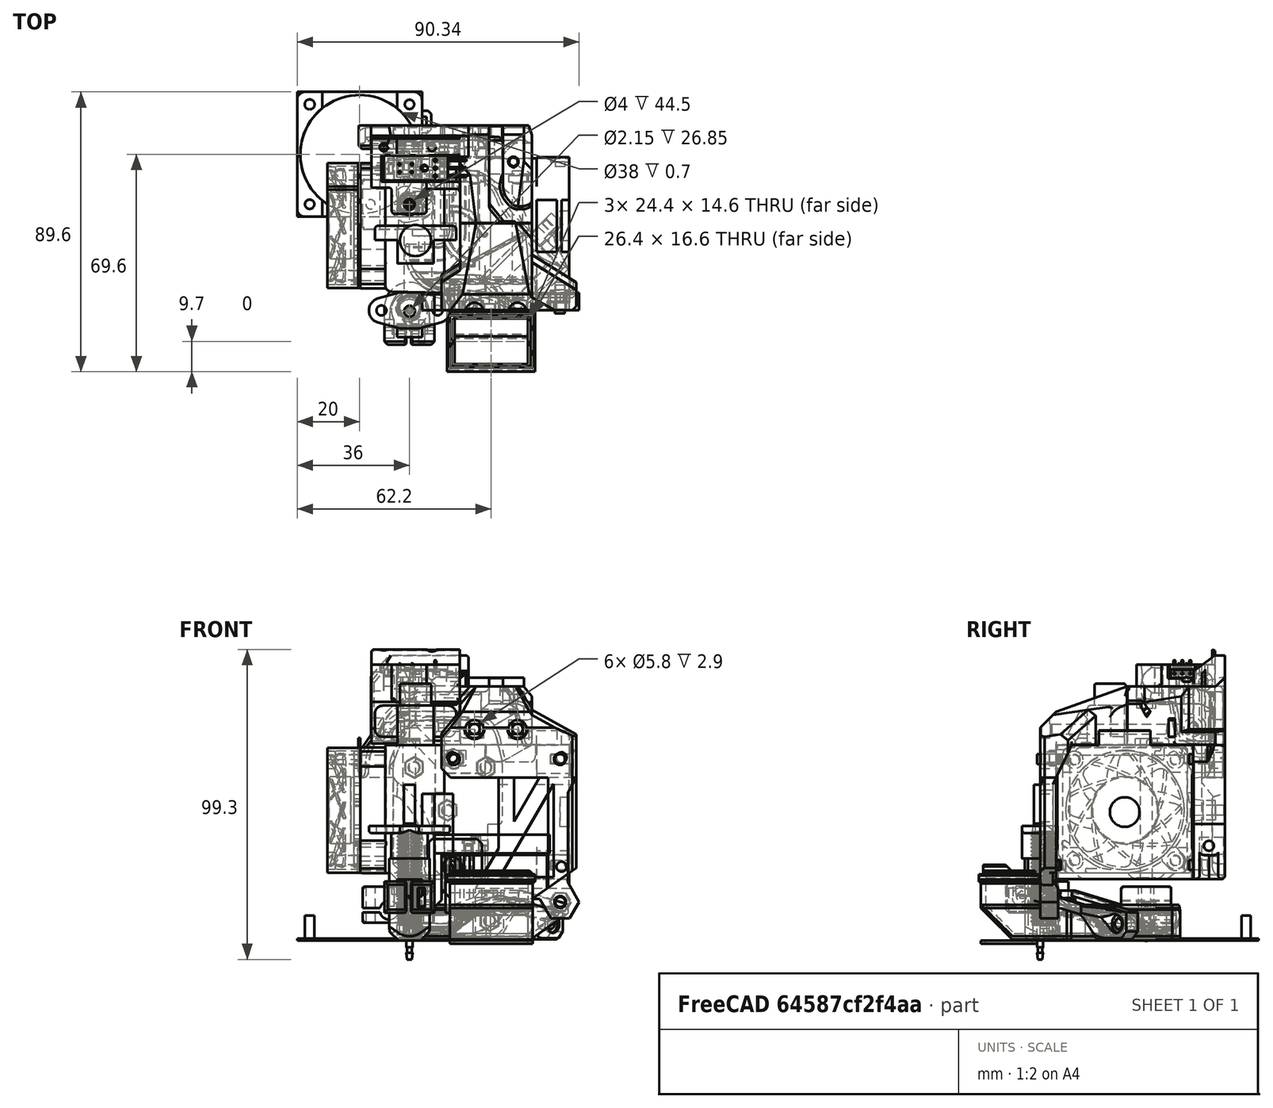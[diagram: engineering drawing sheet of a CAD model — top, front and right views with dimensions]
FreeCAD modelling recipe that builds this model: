
FCSTD DOCUMENT  (FreeCAD 0.18R14555 (Git shallow))
Label: bearmeara-4020-duct
License: All rights reserved
LicenseURL: http://en.wikipedia.org/wiki/All_rights_reserved
objects: Part::Box×57, Part::Cut×48, Part::Feature×41, Part::MultiFuse×32, Part::Cylinder×29, Part::Chamfer×24, Sketcher::SketchObject×6, PartDesign::Body×4, Part::MultiCommon×4, App::DocumentObjectGroup×3, Mesh::Feature×2, PartDesign::AdditiveLoft×2, PartDesign::Pad×2, App::Part×1
note: 253 computed .brp shape members not serialized (recipe doc carries the construction recipe); baked Part::Feature solids carry a one-line shape summary decoded from their .brp

FEATURE [Part::Feature] Part__Feature018  label="NOZZLE-POS"
  Placement = pos=(-0.025,3.1e-14,12.45) rot=(0.707107,0.707107,0;3.14159rad)
  shape: bbox 8.083 x 7 x 12.5 mm, 18 faces (baked)
FEATURE [Part::Feature] Part__Feature012  label="body_front"
  Placement = pos=(-5.275,25.1,21) rot=(0,0,-1;1.5708rad)
  shape: bbox 44.13 x 28.92 x 79.97 mm, 174 faces (baked)
FEATURE [Part::Feature] Part__Feature017  label="v6_heaterblock v1"
  Placement = pos=(-14.9885,-8.00025,5.758) rot=(0,0,1;0rad)
  shape: bbox 23 x 16 x 11.5 mm, 37 faces (baked)
FEATURE [Part::Feature] Part__Feature013  label="stepper"
  Placement = pos=(51.225,-28.9,19.7) rot=(0,0,1;1.5708rad)
  shape: bbox 40 x 44 x 47.7 mm, 101 faces (baked)
FEATURE [Part::Feature] Part__Feature014  label="heatsink"
  Placement = pos=(11.225,-28.4,19.7) rot=(0,0,1;1.5708rad)
  shape: bbox 30.92 x 43.26 x 62.61 mm, 110 faces (baked)
FEATURE [Part::Feature] Part__Feature016  label="e3d_hemera_fan v1"
  Placement = pos=(-15.775,13.2,61.8) rot=(0.57735,-0.57735,0.57735;4.18879rad)
  shape: bbox 10.51 x 40.01 x 40.01 mm, 129 faces (baked)
FEATURE [Mesh::Feature] lower_4020_fan_duct  label="lower_4020-fan-duct"
  Placement = pos=(11.3,-33.9,19.8) rot=(0,0,1;0rad)
FEATURE [Part::Feature] Cut007002001001  label="fan-mount-frame001"
  shape: bbox 28.2 x 19.2 x 3.5 mm, 16 faces (baked)
FEATURE [Part::Feature] Part__Feature  label="duct001"
  Placement = pos=(13,-15,0) rot=(0,0,1;0rad)
  shape: bbox 62.87 x 53.67 x 16.75 mm, 145 faces (baked)
FEATURE [Part::Feature] Part__Feature025  label="duct002"
  Placement = pos=(13,-15,0) rot=(0,0,1;0rad)
  shape: bbox 62.87 x 53.67 x 16.75 mm, 145 faces (baked)
FEATURE [Part::Box] Box  label="Cube"
  AttacherType = Attacher::AttachEngine3D
  Height = 17
  Length = 29
  Placement = pos=(26,-38,0) rot=(0,0,1;0rad)
  Width = 48
FEATURE [Part::Box] Box001  label="Cube001"
  AttacherType = Attacher::AttachEngine3D
  Height = 27
  Length = 26
  Placement = pos=(0,-34,0) rot=(0,0,1;0rad)
  Width = 10
FEATURE [Part::Cut] Cut
  Base = -> Part__Feature
  Tool = -> Box
FEATURE [Part::Cut] Cut007002001002
  Base = -> Cut
  Placement = pos=(0,0,-0.45) rot=(0,0,1;0rad)
  Tool = -> Box001
FEATURE [Part::Box] Box002  label="Cube002"
  AttacherType = Attacher::AttachEngine3D
  Height = 2
  Length = 13
  Placement = pos=(13,-24,0.8) rot=(0,0,1;0rad)
  Width = 4
FEATURE [Part::Box] Box003  label="Cube003"
  AttacherType = Attacher::AttachEngine3D
  Height = 1
  Length = 5
  Placement = pos=(21,-24,0.8) rot=(0,0,1;0rad)
  Width = 13
FEATURE [Part::Cut] Cut007002001003
  Base = -> Cut007002001002
  Tool = -> Box002
FEATURE [Part::Cut] Cut007002001004
  Base = -> Cut007002001003
  Tool = -> Box003
FEATURE [Part::Box] Box004  label="Cube004"
  AttacherType = Attacher::AttachEngine3D
  Height = 10
  Length = 24
  Placement = pos=(7,-30,10) rot=(0,0,1;0rad)
  Width = 27
FEATURE [Part::Cut] Cut007002001005
  Base = -> Cut007002001004
  Tool = -> Box004
FEATURE [Part::Box] Box005  label="Cube005"
  AttacherType = Attacher::AttachEngine3D
  Height = 10
  Length = 32
  Placement = pos=(-2,-38,0) rot=(0,0,1;0rad)
  Width = 14
FEATURE [Part::Box] Box007  label="Cube007"
  AttacherType = Attacher::AttachEngine3D
  Height = 10
  Length = 21
  Placement = pos=(26,-24,0) rot=(0,0,1;0rad)
  Width = 21
FEATURE [Part::Box] Box008  label="Cube008"
  AttacherType = Attacher::AttachEngine3D
  Height = 1
  Length = 41
  Placement = pos=(10,-35,9) rot=(0,0,1;0.506145rad)
  Width = 10
FEATURE [Part::MultiFuse] Fusion
  Shapes = -> [Cut007002001005,Box008]
FEATURE [Part::Cut] Cut007002001006
  Base = -> Fusion
  Tool = -> Box005
FEATURE [Part::Cut] Cut007002001007  label="duct-square-cut"
  Base = -> Cut007002001006
  Tool = -> Box007
FEATURE [Part::Feature] Cut007002001007001  label="Cut007002001008"
  shape: bbox 41.3 x 51.61 x 10 mm, 88 faces (baked)
FEATURE [Part::Box] Box012  label="Cube012"
  AttacherType = Attacher::AttachEngine3D
  Height = 1
  Length = 26.5
  Placement = pos=(13,-53,0) rot=(0,0,1;0rad)
  Width = 18
FEATURE [Part::Box] Box013  label="Cube013"
  AttacherType = Attacher::AttachEngine3D
  Height = 1
  Length = 23.5
  Placement = pos=(14.5,-51.5,0) rot=(0,0,1;0rad)
  Width = 15
FEATURE [Part::Cut] Cut007002001007002
  Base = -> Box012
  Placement = pos=(0,0,-1) rot=(0,0,1;0rad)
  Tool = -> Box013
FEATURE [Sketcher::SketchObject] Sketch
  AttachmentOffset = pos=(0,0,19) rot=(0,0,1;0rad)
  MapMode = 5
  Placement = pos=(0,0,19) rot=(0,0,1;0rad)
  Support = -> [XY_Plane]
  sketch-geometry (8):
    g0: LineSegment StartX=13 StartY=-35 StartZ=0 EndX=39.5 EndY=-35 EndZ=0
    g1: LineSegment StartX=39.5 StartY=-35 StartZ=0 EndX=39.5 EndY=-53 EndZ=0
    g2: LineSegment StartX=39.5 StartY=-53 StartZ=0 EndX=13 EndY=-53 EndZ=0
    g3: LineSegment StartX=13 StartY=-53 StartZ=0 EndX=13 EndY=-35 EndZ=0
    g4: LineSegment StartX=14.5 StartY=-36.5 StartZ=0 EndX=38 EndY=-36.5 EndZ=0
    g5: LineSegment StartX=38 StartY=-36.5 StartZ=0 EndX=38 EndY=-51.5 EndZ=0
    g6: LineSegment StartX=38 StartY=-51.5 StartZ=0 EndX=14.5 EndY=-51.5 EndZ=0
    g7: LineSegment StartX=14.5 StartY=-51.5 StartZ=0 EndX=14.5 EndY=-36.5 EndZ=0
  constraints (16):
    c: Coincident(g0,g1)
    c: Coincident(g1,g2)
    c: Coincident(g2,g3)
    c: Coincident(g3,g0)
    c: Horizontal(g0)
    c: Horizontal(g2)
    c: Vertical(g1)
    c: Vertical(g3)
    c: Coincident(g4,g5)
    c: Coincident(g5,g6)
    c: Coincident(g6,g7)
    c: Coincident(g7,g4)
    c: Horizontal(g4)
    c: Horizontal(g6)
    c: Vertical(g5)
    c: Vertical(g7)
FEATURE [Sketcher::SketchObject] Sketch001
  AttachmentOffset = pos=(0,0,10.45) rot=(0,0,1;0rad)
  MapMode = 5
  Placement = pos=(0,0,10.45) rot=(0,0,1;0rad)
  Support = -> [XY_Plane]
  sketch-geometry (8):
    g0: LineSegment StartX=13 StartY=-53 StartZ=0 EndX=39.5 EndY=-53 EndZ=0
    g1: LineSegment StartX=39.5 StartY=-53 StartZ=0 EndX=39.5 EndY=-24 EndZ=0
    g2: LineSegment StartX=39.5 StartY=-24 StartZ=0 EndX=13 EndY=-24 EndZ=0
    g3: LineSegment StartX=13 StartY=-24 StartZ=0 EndX=13 EndY=-53 EndZ=0
    g4: LineSegment StartX=38 StartY=-25.5 StartZ=0 EndX=14.5 EndY=-25.5 EndZ=0
    g5: LineSegment StartX=14.5 StartY=-25.5 StartZ=0 EndX=14.5 EndY=-51.5 EndZ=0
    g6: LineSegment StartX=14.5 StartY=-51.5 StartZ=0 EndX=38 EndY=-51.5 EndZ=0
    g7: LineSegment StartX=38 StartY=-51.5 StartZ=0 EndX=38 EndY=-25.5 EndZ=0
  constraints (16):
    c: Coincident(g0,g1)
    c: Coincident(g1,g2)
    c: Coincident(g2,g3)
    c: Coincident(g3,g0)
    c: Horizontal(g0)
    c: Horizontal(g2)
    c: Vertical(g1)
    c: Vertical(g3)
    c: Coincident(g4,g5)
    c: Coincident(g5,g6)
    c: Coincident(g6,g7)
    c: Coincident(g7,g4)
    c: Horizontal(g4)
    c: Horizontal(g6)
    c: Vertical(g5)
    c: Vertical(g7)
FEATURE [PartDesign::AdditiveLoft] AdditiveLoft
  Closed = false
  Profile = -> Sketch
  Ruled = false
  Sections = -> [Sketch001]
FEATURE [PartDesign::Body] Body  label="ramp"
  Group = -> [Sketch,Sketch001,AdditiveLoft]
  Origin = -> Origin
  Tip = -> AdditiveLoft
FEATURE [Part::Feature] Body001  label="ramp001"
  Placement = pos=(0,0,-0.45) rot=(0,0,1;0rad)
  shape: bbox 26.5 x 29 x 8.55 mm, 10 faces (baked)
FEATURE [Sketcher::SketchObject] Sketch002  label="Sketch003"
  AttachmentOffset = pos=(0,0,0.45) rot=(0,0,1;0rad)
  MapMode = 5
  Placement = pos=(0,0,0.45) rot=(0,0,1;0rad)
  Support = -> [XY_Plane001]
  sketch-geometry (8):
    g0: LineSegment StartX=39.5 StartY=-24 StartZ=0 EndX=13 EndY=-24 EndZ=0
    g1: LineSegment StartX=13 StartY=-24 StartZ=0 EndX=13 EndY=-43 EndZ=0
    g2: LineSegment StartX=13 StartY=-43 StartZ=0 EndX=39.5 EndY=-43 EndZ=0
    g3: LineSegment StartX=39.5 StartY=-43 StartZ=0 EndX=39.5 EndY=-24 EndZ=0
    g4: LineSegment StartX=38 StartY=-25.5 StartZ=0 EndX=14.5 EndY=-25.5 EndZ=0
    g5: LineSegment StartX=14.5 StartY=-25.5 StartZ=0 EndX=14.5 EndY=-41.5 EndZ=0
    g6: LineSegment StartX=14.5 StartY=-41.5 StartZ=0 EndX=38 EndY=-41.5 EndZ=0
    g7: LineSegment StartX=38 StartY=-41.5 StartZ=0 EndX=38 EndY=-25.5 EndZ=0
  constraints (16):
    c: Coincident(g0,g1)
    c: Coincident(g1,g2)
    c: Coincident(g2,g3)
    c: Coincident(g3,g0)
    c: Horizontal(g0)
    c: Horizontal(g2)
    c: Vertical(g1)
    c: Vertical(g3)
    c: Coincident(g4,g5)
    c: Coincident(g5,g6)
    c: Coincident(g6,g7)
    c: Coincident(g7,g4)
    c: Horizontal(g4)
    c: Horizontal(g6)
    c: Vertical(g5)
    c: Vertical(g7)
FEATURE [Sketcher::SketchObject] Sketch003  label="Sketch004"
  AttachmentOffset = pos=(0,0,10.45) rot=(0,0,1;0rad)
  MapMode = 5
  Placement = pos=(0,0,10.45) rot=(0,0,1;0rad)
  Support = -> [XY_Plane001]
  sketch-geometry (8):
    g0: LineSegment StartX=13 StartY=-24 StartZ=0 EndX=39.5 EndY=-24 EndZ=0
    g1: LineSegment StartX=39.5 StartY=-24 StartZ=0 EndX=39.5 EndY=-53 EndZ=0
    g2: LineSegment StartX=39.5 StartY=-53 StartZ=0 EndX=13 EndY=-53 EndZ=0
    g3: LineSegment StartX=13 StartY=-53 StartZ=0 EndX=13 EndY=-24 EndZ=0
    g4: LineSegment StartX=14.5 StartY=-25.5 StartZ=0 EndX=38 EndY=-25.5 EndZ=0
    g5: LineSegment StartX=38 StartY=-25.5 StartZ=0 EndX=38 EndY=-51.5 EndZ=0
    g6: LineSegment StartX=38 StartY=-51.5 StartZ=0 EndX=14.5 EndY=-51.5 EndZ=0
    g7: LineSegment StartX=14.5 StartY=-51.5 StartZ=0 EndX=14.5 EndY=-25.5 EndZ=0
  constraints (16):
    c: Coincident(g0,g1)
    c: Coincident(g1,g2)
    c: Coincident(g2,g3)
    c: Coincident(g3,g0)
    c: Horizontal(g0)
    c: Horizontal(g2)
    c: Vertical(g1)
    c: Vertical(g3)
    c: Coincident(g4,g5)
    c: Coincident(g5,g6)
    c: Coincident(g6,g7)
    c: Coincident(g7,g4)
    c: Horizontal(g4)
    c: Horizontal(g6)
    c: Vertical(g5)
    c: Vertical(g7)
FEATURE [PartDesign::AdditiveLoft] AdditiveLoft001
  Closed = false
  Profile = -> Sketch003
  Ruled = false
  Sections = -> [Sketch002]
FEATURE [PartDesign::Body] Body002  label="lower-ramp"
  Group = -> [Sketch002,Sketch003,AdditiveLoft001]
  Origin = -> Origin001
  Tip = -> AdditiveLoft001
FEATURE [Part::Feature] Body002002  label="lower-ramp002"
  Placement = pos=(0,0,-0.45) rot=(0,0,1;0rad)
  shape: bbox 26.5 x 29 x 10 mm, 10 faces (baked)
FEATURE [Sketcher::SketchObject] Sketch004  label="Sketch005"
  MapMode = 5
  Support = -> [XY_Plane002]
  sketch-geometry (31):
    g0: GeomPoint X=26 Y=-24 Z=0
    g1: LineSegment StartX=26 StartY=-24 StartZ=0 EndX=1.71 EndY=-24 EndZ=0
    g2: LineSegment StartX=26 StartY=-24 StartZ=0 EndX=26 EndY=8.3 EndZ=0
    g3: LineSegment StartX=13 StartY=-31 StartZ=0 EndX=14.5 EndY=-31 EndZ=0
    g4: LineSegment StartX=14.5 StartY=-31 StartZ=0 EndX=14.5 EndY=-25.5 EndZ=0
    g5: LineSegment StartX=14.5 StartY=-25.5 StartZ=0 EndX=39.5 EndY=-25.5 EndZ=0
    g6: LineSegment StartX=39.5 StartY=-25.5 StartZ=0 EndX=39.5 EndY=-24 EndZ=0
    g7-g12: Circle [constr] x6 (B-spline internal-alignment scaffolding for g13; pole/knot coordinates omitted)
    g13: BSplineCurve PolesCount=6 KnotsCount=4 Degree=3 IsPeriodic=0
    g14-g17: GeomPoint [constr] x4 (B-spline internal-alignment scaffolding for g13; pole/knot coordinates omitted)
    g18-g24: Circle [constr] x7 (B-spline internal-alignment scaffolding for g25; pole/knot coordinates omitted)
    g25: BSplineCurve PolesCount=7 KnotsCount=5 Degree=3 IsPeriodic=0
    g26-g30: GeomPoint [constr] x5 (B-spline internal-alignment scaffolding for g25; pole/knot coordinates omitted)
  constraints (24):
    c: DistanceY(g0,g-1) = 24
    c: DistanceX(g-1,g0) = 26
    c: Coincident(g1,g0)
    c: Horizontal(g1)
    c: Coincident(g2,g0)
    c: Vertical(g2)
    c: Coincident(g3,g4)
    c: Vertical(g4)
    c: Coincident(g4,g5)
    c: Horizontal(g5)
    c: Coincident(g5,g6)
    c: DistanceY(g2,g2) = 32.3
    c: Coincident(g13,g1)
    c: Radius(g7) = 0.6
    c: Equal(g7, g8-g12) x5
    c: Coincident(g13,g3)
    c: InternalAlignment(g7-g12 -> g13) x6
    c: InternalAlignment(g14-g17 -> g13) x4
    c: Coincident(g25,g2)
    c: Radius(g18) = 1
    c: Equal(g18, g19-g24) x6
    c: Coincident(g25,g6)
    c: InternalAlignment(g18-g24 -> g25) x7
    c: InternalAlignment(g26-g30 -> g25) x5
FEATURE [PartDesign::Pad] Pad
  Length = 10
  Length2 = 100
  Profile = -> Sketch004
  Type = 0
FEATURE [PartDesign::Body] Body002003  label="outer"
  Group = -> [Sketch004,Pad]
  Origin = -> Origin002
  Tip = -> Pad
FEATURE [Sketcher::SketchObject] Sketch005  label="Sketch006"
  MapMode = 5
  Support = -> [XY_Plane003]
  sketch-geometry (29):
    g0: GeomPoint X=26 Y=-24 Z=0
    g1: LineSegment StartX=26 StartY=-24 StartZ=0 EndX=3.42 EndY=-24 EndZ=0
    g2: LineSegment StartX=26 StartY=-24 StartZ=0 EndX=26 EndY=6.6 EndZ=0
    g3: GeomPoint X=14.5 Y=-30 Z=0
    g4: GeomPoint X=38 Y=-25.5 Z=0
    g5-g10: Circle [constr] x6 (B-spline internal-alignment scaffolding for g11; pole/knot coordinates omitted)
    g11: BSplineCurve PolesCount=6 KnotsCount=4 Degree=3 IsPeriodic=0
    g12-g15: GeomPoint [constr] x4 (B-spline internal-alignment scaffolding for g11; pole/knot coordinates omitted)
    g16-g21: Circle [constr] x6 (B-spline internal-alignment scaffolding for g22; pole/knot coordinates omitted)
    g22: BSplineCurve PolesCount=6 KnotsCount=4 Degree=3 IsPeriodic=0
    g23-g26: GeomPoint [constr] x4 (B-spline internal-alignment scaffolding for g22; pole/knot coordinates omitted)
    g27: LineSegment StartX=14.5 StartY=-30 StartZ=0 EndX=14.5 EndY=-25.5 EndZ=0
    g28: LineSegment StartX=14.5 StartY=-25.5 StartZ=0 EndX=38 EndY=-25.5 EndZ=0
  constraints (29):
    c: DistanceY(g0,g-1) = 24
    c: DistanceX(g-1,g0) = 26
    c: Coincident(g1,g0)
    c: Horizontal(g1)
    c: Coincident(g2,g0)
    c: Vertical(g2)
    c: DistanceY(g2,g2) = 30.6
    c: DistanceX(g1,g1) = 22.58
    c: DistanceY(g4,g-1) = 25.5
    c: DistanceX(g-1,g4) = 38
    c: DistanceY(g3,g-1) = 30
    c: DistanceX(g-1,g3) = 14.5
    c: Coincident(g11,g1)
    c: Radius(g5) = 0.4
    c: Equal(g5, g6-g10) x5
    c: Coincident(g11,g3)
    c: InternalAlignment(g5-g10 -> g11) x6
    c: InternalAlignment(g12-g15 -> g11) x4
    c: Coincident(g22,g2)
    c: Radius(g16) = 1
    c: Equal(g16, g17-g21) x5
    c: Coincident(g22,g4)
    c: InternalAlignment(g16-g21 -> g22) x6
    c: InternalAlignment(g23-g26 -> g22) x4
    c: Coincident(g27,g3)
    c: Vertical(g27)
    c: Coincident(g28,g27)
    c: Coincident(g28,g4)
    c: Horizontal(g28)
FEATURE [PartDesign::Pad] Pad001
  Length = 8.2
  Length2 = 100
  Profile = -> Sketch005
  Type = 0
FEATURE [PartDesign::Body] Body002004  label="inner"
  Group = -> [Sketch005,Pad001]
  Origin = -> Origin003
  Tip = -> Pad001
FEATURE [App::DocumentObjectGroup] Group001  label="Sketch002"
  Group = -> [Body,Body002,Body002003,Body002004]
FEATURE [Part::Feature] Body002004001  label="inner001"
  Placement = pos=(0,0,0.8) rot=(0,0,1;0rad)
  shape: bbox 34.69 x 36.6 x 8.2 mm, 8 faces (baked)
FEATURE [Part::Box] Box015  label="Cube015"
  AttacherType = Attacher::AttachEngine3D
  Height = 8.2
  Length = 23.5
  Placement = pos=(14.5,-27,0.8) rot=(0,0,1;0rad)
  Width = 5
FEATURE [Part::Box] Box016  label="Cube016"
  AttacherType = Attacher::AttachEngine3D
  Height = 0.8
  Length = 23.5
  Placement = pos=(14.5,-42.5,0) rot=(0,0,1;0rad)
  Width = 18
FEATURE [Part::Feature] Body002003001  label="outer001"
  shape: bbox 37.79 x 39.3 x 10 mm, 10 faces (baked)
FEATURE [Part::Feature] Body002004002  label="inner002"
  Placement = pos=(0,0,0.8) rot=(0,0,1;0rad)
  shape: bbox 34.69 x 36.6 x 8.2 mm, 8 faces (baked)
FEATURE [Part::Feature] Cut007002001007009  label="fan-mount-frame002"
  Placement = pos=(0,0,-0.45) rot=(0,0,1;0rad)
  shape: bbox 28.2 x 19.2 x 3.5 mm, 16 faces (baked)
FEATURE [Part::Cut] Cut007002001007010
  Base = -> Body002003001
  Tool = -> Body002004001
FEATURE [Part::MultiFuse] Fusion001
  Shapes = -> [Box016,Body002002]
FEATURE [Part::Cut] Cut007002001007011
  Base = -> Fusion001
  Tool = -> Box015
FEATURE [Part::Cut] Cut007002001007012
  Base = -> Cut007002001007011
  Tool = -> Body002004002
FEATURE [Part::MultiFuse] Fusion002
  Shapes = -> [Body001,Cut007002001007012]
FEATURE [Part::MultiFuse] Fusion003
  Shapes = -> [Fusion002,Cut007002001007010]
FEATURE [Part::MultiFuse] Fusion004
  Placement = pos=(0,0,1) rot=(0,0,1;0rad)
  Shapes = -> [Fusion003,Cut007002001007001]
FEATURE [Part::Box] Box017  label="Cube017"
  AttacherType = Attacher::AttachEngine3D
  Height = 0.8
  Length = 4
  Placement = pos=(10,-25,1.8) rot=(0,0,1;0rad)
  Width = 4
FEATURE [Part::Box] Box018  label="Cube018"
  AttacherType = Attacher::AttachEngine3D
  Height = 1
  Length = 36.5
  Placement = pos=(5.64694,-26.4947,8.5) rot=(0,0,1;0.488692rad)
  Width = 1
FEATURE [Part::Box] Box019  label="Cube019"
  AttacherType = Attacher::AttachEngine3D
  Height = 1
  Length = 35.5
  Placement = pos=(3.75,-25.25,9.1) rot=(0,0,1;0rad)
  Width = 1
FEATURE [Part::Chamfer] Chamfer005
  Base = -> Box018
  Edges = 1 edges r=0.5: [Edge9]
  Placement = pos=(0,0,1) rot=(0,0,1;0rad)
FEATURE [Part::Cylinder] Cylinder001  label="stepper-screw-pos"
  Angle = 360
  AttacherType = Attacher::AttachEngine3D
  Height = 10
  Placement = pos=(48.73,-25,58.7) rot=(1,0,0;1.5708rad)
  Radius = 1.65
FEATURE [Part::Cylinder] Cylinder002  label="fill"
  Angle = 360
  AttacherType = Attacher::AttachEngine3D
  Height = 5
  Placement = pos=(48.23,-28.9,58.2) rot=(1,0,0;1.5708rad)
  Radius = 3
FEATURE [Part::Cylinder] Cylinder003  label="fill001"
  Angle = 360
  AttacherType = Attacher::AttachEngine3D
  Height = 5
  Placement = pos=(14.23,-28.9,58.2) rot=(1,0,0;1.5708rad)
  Radius = 3
FEATURE [Part::Box] Box020  label="Cube020"
  AttacherType = Attacher::AttachEngine3D
  Height = 4
  Length = 4
  Placement = pos=(10,-28.9,56) rot=(0,0,1;0rad)
  Width = 3
FEATURE [Part::Box] Box021  label="Cube021"
  AttacherType = Attacher::AttachEngine3D
  Height = 6
  Length = 4
  Placement = pos=(48.55,-28.9,55.2) rot=(0,0,1;0rad)
  Width = 5
FEATURE [Part::Cylinder] Cylinder004  label="stepper-screw-pos001"
  Angle = 360
  AttacherType = Attacher::AttachEngine3D
  Height = 10
  Placement = pos=(13.73,-25,58.7) rot=(1,0,0;1.5708rad)
  Radius = 1.65
FEATURE [Part::Cylinder] Cylinder005  label="stepper-screw-pos002"
  Angle = 360
  AttacherType = Attacher::AttachEngine3D
  Height = 10
  Placement = pos=(48.23,-25,58.2) rot=(1,0,0;1.5708rad)
  Radius = 1.6
FEATURE [Part::Cylinder] Cylinder006  label="stepper-screw-pos003"
  Angle = 360
  AttacherType = Attacher::AttachEngine3D
  Height = 10
  Placement = pos=(13.73,-25,25.1) rot=(1,0,0;1.5708rad)
  Radius = 0.5
FEATURE [Part::Cylinder] Cylinder007  label="stepper-screw-pos004"
  Angle = 360
  AttacherType = Attacher::AttachEngine3D
  Height = 10
  Placement = pos=(48.73,-25,23.7) rot=(1,0,0;1.5708rad)
  Radius = 1.6
FEATURE [Part::Feature] Part__Feature012001  label="body_front001"
  Placement = pos=(-5.275,25.1,21) rot=(0,0,-1;1.5708rad)
  shape: bbox 44.13 x 28.92 x 79.97 mm, 174 faces (baked)
FEATURE [Part::Feature] Part__Feature012002  label="body_front002"
  Placement = pos=(-5.275,25.1,21) rot=(0,0,-1;1.5708rad)
  shape: bbox 44.13 x 28.92 x 79.97 mm, 174 faces (baked)
FEATURE [Part::MultiFuse] Fusion008
  Shapes = -> [Part__Feature012002,Cylinder003]
FEATURE [Part::MultiFuse] Fusion009
  Shapes = -> [Fusion008,Cylinder002]
FEATURE [Part::Cut] Cut007002001007014
  Base = -> Fusion009
  Tool = -> Box020
FEATURE [Part::Cut] Cut007002001007015
  Base = -> Cut007002001007014
  Tool = -> Box021
FEATURE [Part::Cut] Cut007002001007016
  Base = -> Cut007002001007015
  Tool = -> Cylinder001
FEATURE [Part::Cut] Cut007002001007017
  Base = -> Cut007002001007016
  Tool = -> Cylinder004
FEATURE [Part::Box] Box022  label="Cube022"
  AttacherType = Attacher::AttachEngine3D
  Height = 5
  Length = 7
  Placement = pos=(11,-31,56) rot=(0,0,1;0rad)
  Width = 10
FEATURE [Part::MultiCommon] Common  label="body-pos-fix"
  Shapes = -> [Box022,Part__Feature012001]
FEATURE [Part::Feature] Common001  label="body-pos-fix001"
  Placement = pos=(0,0,-34) rot=(0,0,1;0rad)
  shape: bbox 7 x 3.1 x 5 mm, 23 faces (baked)
FEATURE [Part::Box] Box023  label="Cube023"
  AttacherType = Attacher::AttachEngine3D
  Height = 10
  Length = 10
  Placement = pos=(4,-28.9,19) rot=(0,0,1;0rad)
  Width = 10
FEATURE [Part::Cut] Cut007002001007018
  Base = -> Common001
  Tool = -> Box023
FEATURE [Part::Cylinder] Cylinder008  label="tmpp"
  Angle = 360
  AttacherType = Attacher::AttachEngine3D
  Height = 2.1
  Placement = pos=(14.23,-28.9,24.2) rot=(1,0,0;1.5708rad)
  Radius = 1.7
FEATURE [Part::MultiFuse] Fusion010  label="body-pos-2"
  Shapes = -> [Cylinder008,Cut007002001007018]
FEATURE [Part::Box] Box024  label="Cube024"
  AttacherType = Attacher::AttachEngine3D
  Height = 14
  Length = 41
  Placement = pos=(10.23,-33.9,13.5) rot=(0,0,1;0rad)
  Width = 5
FEATURE [Part::Cylinder] Cylinder009  label="stepper-screw-pos005"
  Angle = 360
  AttacherType = Attacher::AttachEngine3D
  Height = 12
  Placement = pos=(13.73,-31,26.4) rot=(1,0,0;1.5708rad)
  Radius = 0.5
FEATURE [Part::Feature] Fusion010002  label="body-pos-1"
  Placement = pos=(62.4,0,48.4) rot=(0,1,0;3.14159rad)
  shape: bbox 7 x 3.1 x 5 mm, 25 faces (baked)
FEATURE [Part::Box] Box026  label="Cube026"
  AttacherType = Attacher::AttachEngine3D
  Height = 10
  Length = 30
  Placement = pos=(40.8236,-35.5,2.21194) rot=(0,-1,0;0.610865rad)
  Width = 10
FEATURE [Part::Box] Box027  label="Cube027"
  AttacherType = Attacher::AttachEngine3D
  Height = 10
  Length = 10
  Placement = pos=(51.23,-38,19) rot=(0,0,1;0rad)
  Width = 10
FEATURE [Part::Box] Box028  label="Cube028"
  AttacherType = Attacher::AttachEngine3D
  Height = 29
  Length = 10
  Placement = pos=(44,-41,0) rot=(0,0,1;0rad)
  Width = 10
FEATURE [Part::Cylinder] Cylinder010  label="stepper-screw-pos006"
  Angle = 360
  AttacherType = Attacher::AttachEngine3D
  Height = 10
  Placement = pos=(48.73,-25,25.1) rot=(1,0,0;1.5708rad)
  Radius = 0.5
FEATURE [Part::Cylinder] Cylinder011  label="stepper-screw-pos007"
  Angle = 360
  AttacherType = Attacher::AttachEngine3D
  Height = 10
  Placement = pos=(48.73,-25,23.7) rot=(1,0,0;1.5708rad)
  Radius = 1.6
FEATURE [Part::Cylinder] Cylinder012  label="stepper-screw-pos008"
  Angle = 360
  AttacherType = Attacher::AttachEngine3D
  Height = 12
  Placement = pos=(13.73,-31,23.7) rot=(1,0,0;1.5708rad)
  Radius = 3
FEATURE [Part::Cylinder] Cylinder013  label="stepper-screw-pos009"
  Angle = 360
  AttacherType = Attacher::AttachEngine3D
  Height = 10
  Placement = pos=(13.73,-25,23.7) rot=(1,0,0;1.5708rad)
  Radius = 1.6
FEATURE [Part::Cylinder] Cylinder014  label="stepper-screw-pos010"
  Angle = 360
  AttacherType = Attacher::AttachEngine3D
  Height = 12
  Placement = pos=(13.73,-31.2,23.7) rot=(1,0,0;1.5708rad)
  Radius = 3
FEATURE [Part::Box] Box029  label="Cube029"
  AttacherType = Attacher::AttachEngine3D
  Height = 10
  Length = 10
  Placement = pos=(9,-29,13.8) rot=(0,0,1;0rad)
  Width = 10
FEATURE [Part::Chamfer] Chamfer009
  Base = -> Box029
  Edges = 1 edges r=2: [Edge10]
  Placement = pos=(0,0.1,1) rot=(0,0,1;0rad)
FEATURE [Part::Feature] Chamfer009001  label="Chamfer010"
  Placement = pos=(32,0.1,1) rot=(0,0,1;0rad)
  shape: bbox 10 x 10 x 10 mm, 7 faces (baked)
FEATURE [Part::Box] Box030  label="Cube030"
  AttacherType = Attacher::AttachEngine3D
  Height = 60
  Length = 63
  Placement = pos=(0,-43.2,-7.8) rot=(0,0,1;0rad)
  Width = 30
FEATURE [Part::Cut] Cut007002001007029003002  label="tmp-body-front"
  Base = -> Cut007002001007017
  Tool = -> Box030
FEATURE [Part::Feature] Part__Feature011  label="body_back"
  Placement = pos=(-5.275,25.2,21) rot=(0,0,-1;1.5708rad)
  shape: bbox 55.53 x 31.22 x 71.72 mm, 411 faces (baked)
FEATURE [Part::Feature] Part__Feature020  label="pinda v4_y33"
  Placement = pos=(0.025,-33,5) rot=(0,0,-1;1.5708rad)
  shape: bbox 9.315 x 9.314 x 49.01 mm, 71 faces (baked)
FEATURE [Part::Feature] Box025001  label="Cube031"
  Placement = pos=(0,0,1.5) rot=(0,0,1;0rad)
  shape: bbox 23.5 x 14.03 x 14.03 mm, 6 faces (baked)
FEATURE [Part::MultiFuse] Fusion010008
  Shapes = -> [Cylinder007,Cylinder010]
FEATURE [Part::MultiFuse] Fusion010009
  Shapes = -> [Cylinder013,Cylinder006]
FEATURE [Part::MultiFuse] Fusion010010
  Shapes = -> [Cylinder012,Cylinder009]
FEATURE [Part::Cut] Cut007002001007029003011
  Base = -> Fusion004
  Tool = -> Box017
FEATURE [Part::Chamfer] Chamfer
  Base = -> Box019
  Edges = 1 edges r=0.5: [Edge9]
FEATURE [Part::Cut] Cut007002001007029003013
  Base = -> Box024
  Tool = -> Box025001
FEATURE [Part::Cut] Cut007002001007029003014
  Base = -> Fusion010
  Tool = -> Chamfer009
FEATURE [Part::Cut] Cut007002001007029003015
  Base = -> Fusion010002
  Tool = -> Chamfer009001
FEATURE [Part::MultiFuse] Fusion010014
  Shapes = -> [Cut007002001007029003013,Cut007002001007029003015]
FEATURE [Part::MultiFuse] Fusion010015
  Shapes = -> [Fusion010014,Cut007002001007029003014]
FEATURE [Part::Cut] Cut007002001007029003016
  Base = -> Fusion010015
  Tool = -> Box027
FEATURE [Part::Cut] Cut007002001007029003017
  Base = -> Cut007002001007029003016
  Tool = -> Box028
FEATURE [Part::Cut] Cut007002001007029003018
  Base = -> Cut007002001007029003017
  Tool = -> Fusion010008
FEATURE [Part::Cut] Cut007002001007029003019
  Base = -> Cut007002001007029003018
  Tool = -> Fusion010009
FEATURE [Part::Cut] Cut007002001007029003020
  Base = -> Cut007002001007029003019
  Tool = -> Fusion010010
FEATURE [Part::Cut] Cut007002001007029003021
  Base = -> Cut007002001007029003020
  Tool = -> Box026
FEATURE [Part::MultiFuse] Fusion010016
  Shapes = -> [Cut007002001007029003011,Chamfer]
FEATURE [Part::MultiFuse] Fusion010017
  Placement = pos=(0,0,0.5) rot=(0,0,1;0rad)
  Shapes = -> [Fusion010016,Chamfer005]
FEATURE [Part::Chamfer] Chamfer009002
  Base = -> Cut007002001007009
  Edges = 1 edges r=0.8: [Edge12]
FEATURE [Part::Chamfer] Chamfer009003
  Base = -> Chamfer009002
  Edges = 1 edges r=0.6: [Edge1]
FEATURE [Part::Chamfer] Chamfer009004
  Base = -> Chamfer009003
  Edges = 1 edges r=0.9: [Edge15]
FEATURE [Part::Box] Box025002  label="Cube032"
  AttacherType = Attacher::AttachEngine3D
  Height = 3
  Length = 1
  Placement = pos=(13,-52.2,20.85) rot=(0,0,1;0rad)
  Width = 9
FEATURE [Part::Chamfer] Chamfer009006
  Base = -> Cut007002001007029003021
  Edges = 1 edges r=3: [Edge4]
FEATURE [Part::Chamfer] Chamfer009007
  Base = -> Chamfer009006
  Edges = 2 edges r=1: [Edge3,Edge20]
FEATURE [Part::Feature] Fusion010020001  label="hemera-4020-duct-rev-1-refined"
  shape: bbox 52.67 x 64.46 x 26 mm, 194 faces (baked)
FEATURE [Part::Cylinder] Cylinder
  Angle = 360
  AttacherType = Attacher::AttachEngine3D
  Height = 10
  Radius = 1.6
FEATURE [Part::Cylinder] Cylinder015
  Angle = 360
  AttacherType = Attacher::AttachEngine3D
  Height = 8
  Placement = pos=(0,32,0) rot=(0,0,1;0rad)
  Radius = 1.5
FEATURE [Part::Cylinder] Cylinder016
  Angle = 360
  AttacherType = Attacher::AttachEngine3D
  Height = 8
  Placement = pos=(-32,0,0) rot=(0,0,1;0rad)
  Radius = 1.5
FEATURE [Part::Cylinder] Cylinder017
  Angle = 360
  AttacherType = Attacher::AttachEngine3D
  Height = 10
  Placement = pos=(-32,32,0) rot=(0,0,1;0rad)
  Radius = 1.6
FEATURE [Part::Cylinder] Cylinder018
  Angle = 360
  AttacherType = Attacher::AttachEngine3D
  Height = 10
  Placement = pos=(-16,16,0) rot=(0,0,1;0rad)
  Radius = 19
FEATURE [Part::Box] Box025003  label="Cube033"
  AttacherType = Attacher::AttachEngine3D
  Height = 0.7
  Length = 40
  Placement = pos=(-36,-4,0) rot=(0,0,1;0rad)
  Width = 40
FEATURE [Part::Cut] Cut007002001007029003024
  Base = -> Box025003
  Tool = -> Cylinder017
FEATURE [Part::Cut] Cut007002001007029003025
  Base = -> Cut007002001007029003024
  Tool = -> Cylinder
FEATURE [Part::Cut] Cut007002001007029003026
  Base = -> Cut007002001007029003025
  Tool = -> Cylinder018
FEATURE [Part::Feature] Fillet001
  shape: bbox 40 x 40 x 0.7 mm, 13 faces (baked)
FEATURE [Part::Feature] Fillet002
  shape: bbox 40 x 40 x 0.7 mm, 13 faces (baked)
FEATURE [Part::Box] Box025004  label="Cube034"
  AttacherType = Attacher::AttachEngine3D
  Height = 10
  Length = 8
  Placement = pos=(-4,-4,0) rot=(0,0,1;0rad)
  Width = 40
FEATURE [Part::Box] Box025005  label="Cube035"
  AttacherType = Attacher::AttachEngine3D
  Height = 10
  Length = 8
  Placement = pos=(-36,-4,0) rot=(0,0,1;0rad)
  Width = 40
FEATURE [Part::MultiCommon] Common002  label="fan-spacer-lower-tmp"
  Shapes = -> [Box025005,Fillet001]
FEATURE [Part::MultiCommon] Common003
  Shapes = -> [Fillet002,Box025004]
FEATURE [Part::Box] Box025006  label="Cube036"
  AttacherType = Attacher::AttachEngine3D
  Height = 0.7
  Length = 3
  Placement = pos=(4,0,0) rot=(0,0,1;0rad)
  Width = 7
FEATURE [Part::Box] Box025007  label="Cube037"
  AttacherType = Attacher::AttachEngine3D
  Height = 0.7
  Length = 1.5
  Placement = pos=(4,2,0) rot=(0,0,1;0rad)
  Width = 3
FEATURE [Part::MultiFuse] Fusion010020005  label="fan-spacer-lower"
  Shapes = -> [Common002,Cylinder016]
FEATURE [Part::Cut] Cut007002001007029003027
  Base = -> Box025006
  Tool = -> Box025007
FEATURE [Part::Chamfer] Chamfer009008
  Base = -> Cut007002001007029003027
  Edges = 2 edges r=1: [Edge20,Edge24]
FEATURE [Part::Feature] Chamfer009008001  label="Chamfer009009"
  Placement = pos=(0,23,0) rot=(0,0,1;0rad)
  shape: bbox 3 x 7 x 0.7 mm, 12 faces (baked)
FEATURE [Part::MultiFuse] Fusion010020006  label="fan-spacer-upper"
  Shapes = -> [Common003,Chamfer009008,Chamfer009008001,Cylinder015]
FEATURE [App::DocumentObjectGroup] Group002  label="export"
  Group = -> [Fusion010020006,Fusion010020005]
FEATURE [Mesh::Feature] turbo_fan_35x18_2_  label="4020-fan"
  Placement = pos=(31.25,-53.5,41.25) rot=(1,0,0;1.5708rad)
FEATURE [Part::Box] Box025009  label="Cube039"
  AttacherType = Attacher::AttachEngine3D
  Height = 1
  Length = 36
  Placement = pos=(10.5,-35.6,20.85) rot=(0,0,1;0rad)
  Width = 1.3
FEATURE [Part::Box] Box025010  label="Cube040"
  AttacherType = Attacher::AttachEngine3D
  Height = 1
  Length = 2
  Placement = pos=(11,-56.6,20.85) rot=(0,0,1;0rad)
  Width = 21.3
FEATURE [Part::Box] Box025011  label="Cube041"
  AttacherType = Attacher::AttachEngine3D
  Height = 1
  Length = 2
  Placement = pos=(39.5,-56.6,20.85) rot=(0,0,1;0rad)
  Width = 21.3
FEATURE [Part::Box] Box025012  label="Cube042"
  AttacherType = Attacher::AttachEngine3D
  Height = 1
  Length = 36
  Placement = pos=(10.5,-54.5,20.85) rot=(0,0,1;0rad)
  Width = 2.3
FEATURE [Part::Cut] Cut007002001007029003028
  Base = -> Fusion010020001
  Tool = -> Box025009
FEATURE [Part::Cut] Cut007002001007029003029
  Base = -> Cut007002001007029003028
  Tool = -> Box025010
FEATURE [Part::Cut] Cut007002001007029003030
  Base = -> Cut007002001007029003029
  Tool = -> Box025011
FEATURE [Part::Cut] Cut007002001007029003031
  Base = -> Cut007002001007029003030
  Tool = -> Box025012
FEATURE [Part::Feature] Cut007002001002005001  label="fan-mount-frame-lower"
  Placement = pos=(11.7,-54,18.85) rot=(0,0,1;0rad)
  shape: bbox 28.2 x 19.2 x 3.5 mm, 16 faces (baked)
FEATURE [Part::Feature] Cut007002001007029003032  label="fan-mount-frame-lower001"
  Placement = pos=(11.7,-54,18.85) rot=(0,0,1;0rad)
  shape: bbox 28.2 x 19.2 x 3.5 mm, 16 faces (baked)
FEATURE [Part::Chamfer] Chamfer009008005
  Base = -> Fusion010017
  Edges = 2 edges r=1: [Edge5,Edge7]
FEATURE [Part::Chamfer] Chamfer009008006
  Base = -> Box025002
  Edges = 1 edges r=1.5: [Edge12]
FEATURE [Part::MultiFuse] Fusion010020007
  Shapes = -> [Cut007002001007029003032,Chamfer009008006]
FEATURE [Part::Chamfer] Chamfer009008007
  Base = -> Fusion010020007
  Edges = 1 edges r=0.9: [Edge4]
FEATURE [Part::Chamfer] Chamfer009008008
  Base = -> Chamfer009008007
  Edges = 1 edges r=0.6: [Edge5]
FEATURE [Part::Chamfer] Chamfer009008009
  Base = -> Chamfer009008008
  Edges = 1 edges r=0.8: [Edge15]
FEATURE [Part::Cut] Cut007002001007029003033
  Base = -> Chamfer009008009
  Tool = -> Cylinder014
FEATURE [Part::MultiFuse] Fusion010020008
  Shapes = -> [Cut007002001007029003033,Chamfer009008005]
FEATURE [Part::MultiFuse] Fusion010020009  label="duct-rev-2"
  Shapes = -> [Fusion010020008,Chamfer009007]
FEATURE [Part::Feature] Fusion010020005001  label="fan-spacer-lower001"
  Placement = pos=(-16,-22.75,57.75) rot=(0,-1,0;1.5708rad)
  shape: bbox 8 x 40 x 8 mm, 13 faces (baked)
FEATURE [Part::Feature] Fusion010020006001  label="fan-spacer-upper001"
  Placement = pos=(-15.7,-22.75,58) rot=(0,-1,0;1.5708rad)
  shape: bbox 8 x 40 x 11 mm, 33 faces (baked)
FEATURE [Part::Box] Box025013  label="Cube043"
  AttacherType = Attacher::AttachEngine3D
  Height = 36
  Length = 9
  Placement = pos=(44.45,-33.9,16.64) rot=(0,0,1;0rad)
  Width = 5
FEATURE [Part::Chamfer] Chamfer009008010
  Base = -> Box025013
  Edges = 1 edges r=1.3: [Edge5]
FEATURE [Part::Cut] Cut007002001007029003034
  Base = -> Chamfer009008010
  Tool = -> Cylinder011
FEATURE [Part::Feature] Box025014001  label="Cube045"
  Placement = pos=(-6.4,0,14.95) rot=(0,0,1;0rad)
  shape: bbox 24.82 x 24 x 25.31 mm, 6 faces (baked)
FEATURE [Part::Cut] Cut007002001007029003035
  Base = -> Cut007002001007029003034
  Tool = -> Box025014001
FEATURE [Part::Box] Box025014002  label="Cube046"
  AttacherType = Attacher::AttachEngine3D
  Height = 12
  Length = 8
  Placement = pos=(43.3,-31.1,15.6) rot=(0,0,1;0rad)
  Width = 3
FEATURE [Part::Cut] Cut007002001007029003036
  Base = -> Cut007002001007029003035
  Tool = -> Box025014002
FEATURE [Part::MultiFuse] Fusion010020009002  label="front-rev-1"
  Shapes = -> [Cut007002001007029003002,Cut007002001007029003036]
FEATURE [Part::Cylinder] Cylinder019
  Angle = 360
  AttacherType = Attacher::AttachEngine3D
  Height = 10
  Placement = pos=(0,-33,10) rot=(0,0,1;0rad)
  Radius = 8
FEATURE [Part::Cylinder] Cylinder020
  Angle = 360
  AttacherType = Attacher::AttachEngine3D
  Height = 10
  Placement = pos=(0,-33,9) rot=(0,0,1;0rad)
  Radius = 4
FEATURE [Part::Box] Box025014003  label="Cube047"
  AttacherType = Attacher::AttachEngine3D
  Height = 10
  Length = 16
  Placement = pos=(-8,-45,10) rot=(0,0,1;0rad)
  Width = 12
FEATURE [Part::Box] Box025014004  label="Cube048"
  AttacherType = Attacher::AttachEngine3D
  Height = 11
  Length = 1.5
  Placement = pos=(-1,-46,9) rot=(0,0,1;0rad)
  Width = 12
FEATURE [Part::MultiFuse] Fusion010020009003
  Placement = pos=(0,0,-1) rot=(0,0,1;0rad)
  Shapes = -> [Box025014003,Cylinder019]
FEATURE [Part::Box] Box025014006  label="Cube050"
  AttacherType = Attacher::AttachEngine3D
  Height = 37
  Length = 4
  Placement = pos=(4,-33.9,10) rot=(0,0,1;0rad)
  Width = 5
FEATURE [Part::Box] Box025014007  label="Cube051"
  AttacherType = Attacher::AttachEngine3D
  Height = 19
  Length = 6
  Placement = pos=(8,-33.9,28) rot=(0,0,1;0rad)
  Width = 5
FEATURE [Part::Box] Box025014009  label="Cube053"
  AttacherType = Attacher::AttachEngine3D
  Height = 6
  Length = 37
  Placement = pos=(8,-33.9,28) rot=(0,0,1;0rad)
  Width = 5
FEATURE [Part::Cylinder] Cylinder021
  Angle = 360
  AttacherType = Attacher::AttachEngine3D
  Height = 20
  Placement = pos=(11,-40,15) rot=(0,-1,0;1.5708rad)
  Radius = 1.6
FEATURE [Part::Cylinder] Cylinder022
  Angle = 360
  AttacherType = Attacher::AttachEngine3D
  Height = 3
  Placement = pos=(-5,-40,17.8) rot=(0,-1,0;1.5708rad)
  Radius = 0.5
FEATURE [Part::Cylinder] Cylinder023
  Angle = 360
  AttacherType = Attacher::AttachEngine3D
  Height = 20
  Placement = pos=(11,-40,16.4) rot=(0,-1,0;1.5708rad)
  Radius = 0.5
FEATURE [Part::Cylinder] Cylinder024
  Angle = 360
  AttacherType = Attacher::AttachEngine3D
  Height = 3
  Placement = pos=(-5,-40,15) rot=(0,-1,0;1.5708rad)
  Radius = 3
FEATURE [Part::Box] Box025014010  label="Cube054"
  AttacherType = Attacher::AttachEngine3D
  Height = 6
  Length = 2
  Placement = pos=(3,-46,11) rot=(0,0,1;0rad)
  Width = 9
FEATURE [Part::MultiFuse] Fusion010020009004
  Placement = pos=(0,0,-1) rot=(0,0,1;0rad)
  Shapes = -> [Cylinder024,Cylinder022]
FEATURE [Part::MultiFuse] Fusion010020009005
  Placement = pos=(0,0,-1) rot=(0,0,1;0rad)
  Shapes = -> [Cylinder021,Cylinder023]
FEATURE [Part::Box] Box025014011  label="probe-mount-pos-arm"
  AttacherType = Attacher::AttachEngine3D
  Height = 6
  Length = 6
  Placement = pos=(5.23,-32.4,15) rot=(0,0,1;0rad)
  Width = 2
FEATURE [Part::Box] Box025014012  label="probe-mount-pos-arm001"
  AttacherType = Attacher::AttachEngine3D
  Height = 10
  Length = 6
  Placement = pos=(5.23,-32.5,10) rot=(0,0,1;0rad)
  Width = 2.2
FEATURE [Part::Chamfer] Chamfer009008015
  Base = -> Box025014012
  Edges = 1 edges r=2: [Edge6]
  Placement = pos=(0,0,2.3) rot=(0,0,1;0rad)
FEATURE [Part::Box] Box025014013  label="Cube055"
  AttacherType = Attacher::AttachEngine3D
  Height = 19
  Length = 5
  Placement = pos=(5.23,-33.9,9) rot=(0,0,1;0rad)
  Width = 5
FEATURE [Part::Cut] Cut007002001007029003042
  Base = -> Fusion010020009
  Tool = -> Chamfer009008015
FEATURE [Part::Chamfer] Chamfer009008018
  Base = -> Box025014011
  Edges = 2 edges r=1: [Edge6,Edge8]
FEATURE [Part::Box] Box025014014  label="Cube056"
  AttacherType = Attacher::AttachEngine3D
  Height = 5
  Length = 18
  Placement = pos=(5.23,-33.9,27.5) rot=(0,0,1;0rad)
  Width = 5
FEATURE [Part::Cylinder] Cylinder025
  Angle = 360
  AttacherType = Attacher::AttachEngine3D
  Height = 14
  Placement = pos=(19,-31.4,21) rot=(0,0,1;0rad)
  Radius = 0.9
FEATURE [Part::Cylinder] Cylinder026
  Angle = 360
  AttacherType = Attacher::AttachEngine3D
  Height = 14
  Placement = pos=(19,-31.4,25) rot=(0,0,1;0rad)
  Radius = 1
FEATURE [Part::Cylinder] Cylinder027
  Angle = 360
  AttacherType = Attacher::AttachEngine3D
  Height = 2
  Placement = pos=(19,-31.4,31) rot=(0,0,1;0rad)
  Radius = 2
FEATURE [Part::Chamfer] Chamfer009008024
  Base = -> Box025014013
  Edges = 1 edges r=4: [Edge8]
FEATURE [Part::Cut] Cut007002001007029003046  label="fan-duct-rev-2"
  Base = -> Cut007002001007029003042
  Tool = -> Cylinder025
FEATURE [Part::Feature] Cut007002001007029003046001  label="fan-duct-rev-2-refined"
  shape: bbox 52.67 x 64.46 x 26 mm, 198 faces (baked)
FEATURE [Part::Cut] Cut007002001007029003046002
  Base = -> Box025014014
  Tool = -> Cylinder026
FEATURE [Part::Chamfer] Chamfer009008025
  Base = -> Cut007002001007029003046002
  Edges = 1 edges r=1.5: [Edge9]
FEATURE [Part::Chamfer] Chamfer009008026
  Base = -> Chamfer009008025
  Edges = 1 edges r=2: [Edge15]
FEATURE [Part::Cut] Cut007002001007029003046003
  Base = -> Chamfer009008026
  Tool = -> Cylinder027
FEATURE [Part::MultiFuse] Fusion010020009006
  Shapes = -> [Chamfer009008024,Chamfer009008018,Cut007002001007029003046003]
FEATURE [Part::Chamfer] Chamfer009008027
  Base = -> Fusion010020009006
  Edges = 2 edges r=1: [Edge11,Edge19]
FEATURE [Part::Box] Box025014015  label="Cube057"
  AttacherType = Attacher::AttachEngine3D
  Height = 18.3
  Length = 1.7
  Placement = pos=(11.53,-33.9,9) rot=(0,0,1;0rad)
  Width = 5
FEATURE [Part::Feature] Fusion010020009002001  label="front-rev-1-refined"
  shape: bbox 43.24 x 28.92 x 64.47 mm, 118 faces (baked)
FEATURE [Part::Box] Box025014016  label="Cube058"
  AttacherType = Attacher::AttachEngine3D
  Height = 2.8
  Length = 5
  Placement = pos=(10,3,1.5) rot=(0,0,1;0rad)
  Width = 2
FEATURE [Part::Box] Box025014017  label="Cube059"
  AttacherType = Attacher::AttachEngine3D
  Height = 2.8
  Length = 5
  Placement = pos=(10,-8,1.5) rot=(0,0,1;0rad)
  Width = 2
FEATURE [Part::Box] Box025014018  label="Cube060"
  AttacherType = Attacher::AttachEngine3D
  Height = 2.8
  Length = 2
  Placement = pos=(3,-15,1.5) rot=(0,0,1;0rad)
  Width = 5
FEATURE [Part::Box] Box025014019  label="Cube061"
  AttacherType = Attacher::AttachEngine3D
  Height = 1
  Length = 2
  Placement = pos=(10,-10,1.5) rot=(0,0,1;0rad)
  Width = 17
FEATURE [Part::Box] Box025014020  label="Cube062"
  AttacherType = Attacher::AttachEngine3D
  Height = 1
  Length = 10
  Placement = pos=(1,-10,1.5) rot=(0,0,1;0rad)
  Width = 2
FEATURE [Part::MultiFuse] Fusion010020009007003  label="fan-support"
  Shapes = -> [Box025014016,Box025014019,Box025014017,Box025014020,Box025014018]
FEATURE [Part::MultiFuse] Fusion010020009007004  label="fan-w-support"
  Shapes = -> [Cut007002001007029003046001,Fusion010020009007003]
FEATURE [Part::MultiFuse] Fusion010020009007005
  Shapes = -> [Fusion010020009004,Fusion010020009005]
FEATURE [Part::Cut] Cut007002001007029003046004
  Base = -> Fusion010020009003
  Tool = -> Cylinder020
FEATURE [Part::Cut] Cut007002001007029003046005
  Base = -> Cut007002001007029003046004
  Tool = -> Fusion010020009007005
FEATURE [Part::Chamfer] Chamfer009008028
  Base = -> Cut007002001007029003046005
  Edges = 4 edges r=1: [Edge1,Edge8,Edge9,Edge10]
FEATURE [Part::Box] Box025014021  label="Cube063"
  AttacherType = Attacher::AttachEngine3D
  Height = 18.3
  Length = 1.7
  Placement = pos=(14.53,-33.9,9) rot=(0,0,1;0rad)
  Width = 5
FEATURE [Part::Box] Box025014022  label="Cube064"
  AttacherType = Attacher::AttachEngine3D
  Height = 18.3
  Length = 1.7
  Placement = pos=(17.53,-33.9,9) rot=(0,0,1;0rad)
  Width = 5
FEATURE [Part::Box] Box025014023  label="Cube065"
  AttacherType = Attacher::AttachEngine3D
  Height = 18.3
  Length = 2.7
  Placement = pos=(20.53,-33.9,9) rot=(0,0,1;0rad)
  Width = 5
FEATURE [Part::MultiFuse] Fusion010020009007006002  label="probe-custom-support"
  Shapes = -> [Box025014015,Box025014021,Box025014022,Box025014023]
FEATURE [Part::Cylinder] Cylinder028
  Angle = 360
  AttacherType = Attacher::AttachEngine3D
  Height = 19
  Placement = pos=(0,-33,0) rot=(0,0,1;0rad)
  Radius = 4.05
FEATURE [Part::Cut] Cut007002001007029003046006
  Base = -> Chamfer009008028
  Tool = -> Cylinder028
FEATURE [Part::Cut] Cut007002001007029003046007
  Base = -> Cut007002001007029003046006
  Tool = -> Box025014004
FEATURE [Part::Cut] Cut007002001007029003046008
  Base = -> Cut007002001007029003046007
  Tool = -> Box025014010
FEATURE [Part::Chamfer] Chamfer009008029
  Base = -> Cut007002001007029003046008
  Edges = 1 edges r=1: [Edge33]
FEATURE [Part::Chamfer] Chamfer009008030
  Base = -> Chamfer009008029
  Edges = 23 edges r=0.4: [Edge1,Edge2,Edge4,Edge7,Edge8,Edge9,Edge10,Edge11,Edge16,Edge20,Edge21,Edge23,Edge46,Edge47,Edge48,Edge53,Edge62,Edge64,Edge65,Edge66,Edge67,Edge87,Edge88]
FEATURE [Part::MultiFuse] Fusion010020009007006003  label="probe-mount-rev2"
  Shapes = -> [Chamfer009008030,Chamfer009008027]
FEATURE [Part::Feature] Fusion010020009007006003001  label="probe-mount-rev2-rf"
  shape: bbox 31.23 x 20 x 23.5 mm, 72 faces (baked)
FEATURE [Part::MultiFuse] Fusion010020009007006003002
  Shapes = -> [Fusion010020009007006003001,Fusion010020009007006002]
FEATURE [Part::Feature] Part__Feature012003  label="Body"
  shape: bbox 26.66 x 16.68 x 36.75 mm, 74 faces (baked)
FEATURE [Part::Feature] Part__Feature012004  label="Pin"
  shape: bbox 2.652 x 2.652 x 32.75 mm, 7 faces (baked)
FEATURE [App::Part] BLTouch_v3  label="BLTouch v3"
  Group = -> [Part__Feature012003,Part__Feature012004]
  Origin = -> Origin004
FEATURE [Part::MultiFuse] Fusion010020009007006003003  label="bl-touch"
  Placement = pos=(0,-34,36.75) rot=(0,0,1;0rad)
  Shapes = -> [Part__Feature012003,Part__Feature012004]
FEATURE [Part::Feature] Part__Feature001001  label="sensor-part"
  Placement = pos=(-0.0161464,-1.00251,88.44) rot=(0.57735,-0.57735,-0.57735;2.0944rad)
  shape: bbox 17.75 x 31.12 x 29.62 mm, 84 faces (baked)
FEATURE [Part::Feature] Part__Feature002  label="sensor-body"
  Placement = pos=(-142.28,20.0964,82.5032) rot=(0,0,1;0rad)
  shape: bbox 59.85 x 37.16 x 73.13 mm, 621 faces (baked)
FEATURE [Part::Box] Box025014024  label="Cube066"
  AttacherType = Attacher::AttachEngine3D
  Height = 30
  Length = 33
  Placement = pos=(-16.92,0,64.04) rot=(0,0,1;0rad)
  Width = 22
FEATURE [Part::Feature] Part__Feature006001  label="IR-sensor-002"
  Placement = pos=(69.5,24,-25) rot=(-0.57735,0.57735,0.57735;4.18879rad)
  shape: bbox 26.54 x 8 x 8.2 mm, 246 faces, 11 solids (baked)
FEATURE [App::DocumentObjectGroup] Group  label="Preference"
  Group = -> [Part__Feature018,Part__Feature017,Part__Feature013,Part__Feature014,Part__Feature016,lower_4020_fan_duct,Cut007002001001,Cut007002001007,Cylinder005,Part__Feature012,Common,Part__Feature020,turbo_fan_35x18_2_,Cut007002001002005001,Cut007002001007029003046,Fusion010020009002,BLTouch_v3,Fusion010020009007006003003,Part__Feature006001]
FEATURE [Part::MultiCommon] Common004
  Shapes = -> [Part__Feature002,Box025014024]
